# Revit family: Haworth_Epure_DoubleWorkstationDesk_AP_PRELIMINARY
name_source: partatom
category: Furniture
units: mm (PartAtom-declared; Revit-internal decimal feet)

## family parameters
Always vertical = Yes
Cut with Voids When Loaded = No
OmniClass Number = 23.40.70.14.64.11
OmniClass Title = Office Furniture
Room Calculation Point = No
Shared = No
Work Plane-Based = No

## types (6) — shared parameters
Actual Height = 730 mm  [stored 2.39501 ft]
Assembly Code = E2020200
Cable Tray Finish = Haworth _ Polymer _ Undecided
Description = Haworth - Epure - Double Workstation
Flip Top Finish = Haworth _ Paint _ Metallic Silver
Leg Height = 695 mm  [stored 2.28018 ft]
Manufacturer = Haworth
Model = SYEPDW1XXX
Revision Number = 1
Size = Verify Final Dim.w/ Haworth
Top Gap Depth = 30 mm  [stored 0.0984252 ft]
Trim Finish = Haworth _ Metal _ Structured White EC
URL = https://www.haworth.com
URL - Product = https://www.haworth.com
Warranty = http://www.haworth.com
Worksurface Depth = 1200, 1400, 1500, 1600 mm
Worksurface Width = 1200, 1400, 1500, 1600, 1800 mm

## per-type parameters (varying)
| type | Accessory Kit | Actual Depth | Actual Width | Aluminium Legs | Cable Tray | Cable Tray Width | Depth | Flip Top Cable Outlet | No Accessory Kit | Round Cable Outlet | Umbilical Cord | Wooden Legs | with Fixing Kit | with Screen Gap | without Screen Gap |
| 1800 x 1600 | Yes | 1600 mm  [stored 5.24934 ft] | 1800 mm  [stored 5.90551 ft] | No | Yes | 1300 mm  [stored 4.26509 ft] | 785 mm | No | No | Yes | Yes | Yes | Yes | Yes | No |
| 1200 x 1200 | No | 1200 mm | 1200 mm | Yes | No | 700 mm | 600 mm | No | Yes | No | No | No | No | No | Yes |
| 1500 x 1400 | No | 1400 mm | 1500 mm  [stored 4.92126 ft] | No | No | 1000 mm  [stored 3.28084 ft] | 685 mm | No | Yes | No | No | Yes | Yes | Yes | No |
| 1200 x 1500 | Yes | 1500 mm  [stored 4.92126 ft] | 1200 mm | No | Yes | 700 mm | 735 mm | No | No | No | No | Yes | No | Yes | No |
| 1600 x 1500 | Yes | 1500 mm  [stored 4.92126 ft] | 1600 mm  [stored 5.24934 ft] | Yes | No | 1100 mm | 750 mm  [stored 2.46063 ft] | Yes | No | No | Yes | No | Yes | No | Yes |
| 1400 x 1600 | Yes | 1600 mm  [stored 5.24934 ft] | 1400 mm | Yes | No | 900 mm  [stored 2.95276 ft] | 800 mm  [stored 2.62467 ft] | Yes | No | No | Yes | No | Yes | No | Yes |

note: [stored X ft] marks values corroborated as IEEE doubles in the binary element streams (Revit-internal decimal feet)

## geometry (parser evidence)
native form markers: Sweep x30
no freeform markers — native parametric forms only
